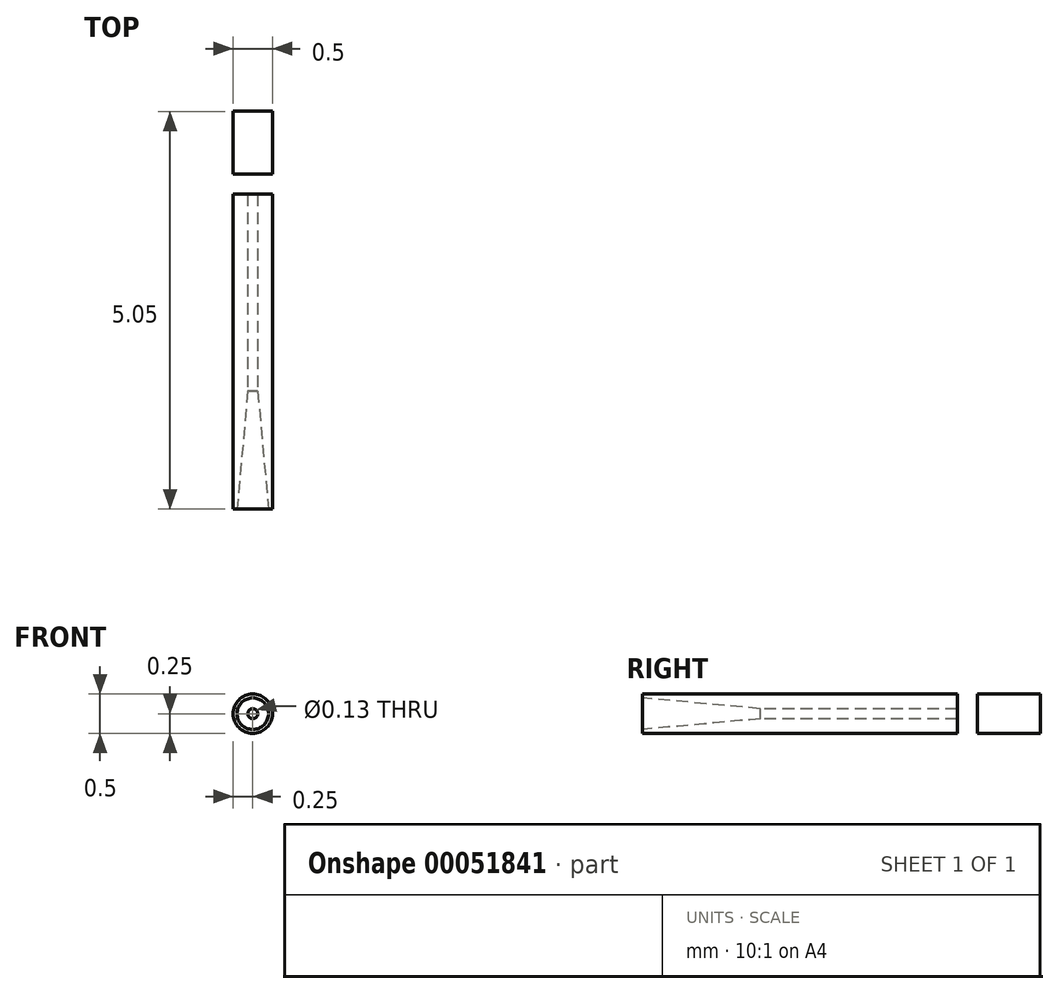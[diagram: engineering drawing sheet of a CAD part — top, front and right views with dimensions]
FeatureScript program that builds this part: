
annotation { "Feature Type Name" : "Feature", "Feature Type Description" : "" }
export const myFeature = defineFeature(function(context is Context, id is Id, definition is map)
    precondition{}
    {
        {
            var Q0;
            Q0=qCreatedBy(makeId("Right.planeOp"),FACE);
            var sketch = newSketch(context, id + "F0", { "sketchPlane" : qUnion([Q0])});
            skLineSegment(sketch, "E0.top", {"start": v(0, 0.25) * mm, "end": v(4, 0.25) * mm});
            skLineSegment(sketch, "E0.left", {"start": v(0, 0.2) * mm, "end": v(0, 0.25) * mm});
            skLineSegment(sketch, "E0.right", {"start": v(4, 0.06) * mm, "end": v(4, 0.25) * mm});
            skLineSegment(sketch, "E1.top", {"start": v(1.5, 0.06) * mm, "end": v(4, 0.06) * mm});
            skLineSegment(sketch, "E2", {"start": v(0, 0.2) * mm, "end": v(1.5, 0.06) * mm});
            skLineSegment(sketch, "E3", {"start": v(0, 0) * mm, "end": v(4.16, 0) * mm, "construction": true});
            skSolve(sketch);
        }
        {
            var Q0;
            Q0 = qSketchRegion(id + "F0", true);
            var Q1;
            Q1=sQuery(id+"F0.wireOp",EDGE,"E3");
            revolve(context, id + "F1", {"entities" : qUnion([Q0]), "axis" : qUnion([Q1]), "revolveType" : RevolveType.FULL});
        }
        {
            var Q0;
            Q0=qCreatedBy(makeId("Right.planeOp"),FACE);
            var sketch = newSketch(context, id + "F2", { "sketchPlane" : qUnion([Q0])});
            skLineSegment(sketch, "E4.bottom", {"start": v(4.25, 0) * mm, "end": v(5.05, 0) * mm});
            skLineSegment(sketch, "E4.top", {"start": v(4.25, 0.25) * mm, "end": v(5.05, 0.25) * mm});
            skLineSegment(sketch, "E4.left", {"start": v(4.25, 0) * mm, "end": v(4.25, 0.25) * mm});
            skLineSegment(sketch, "E4.right", {"start": v(5.05, 0) * mm, "end": v(5.05, 0.25) * mm});
            skSolve(sketch);
        }
        {
            var Q0;
            Q0 = qSketchRegion(id + "F2", true);
            var Q1;
            Q1=sQuery(id+"F2.wireOp",EDGE,"E4.bottom");
            revolve(context, id + "F3", {"entities" : qUnion([Q0]), "axis" : qUnion([Q1]), "revolveType" : RevolveType.FULL});
        }
    });
